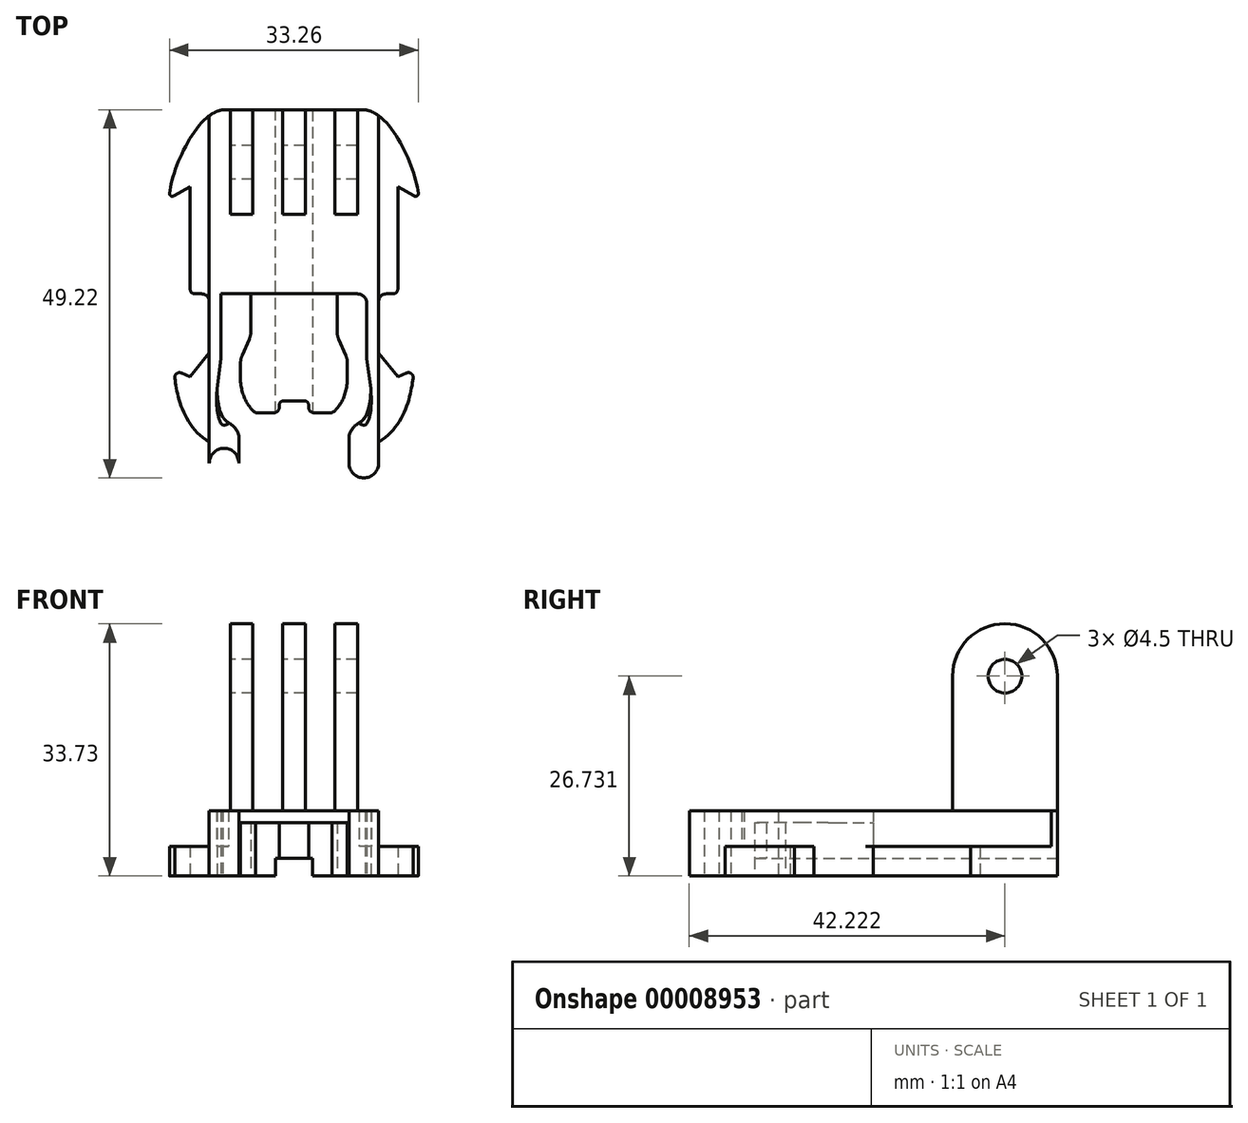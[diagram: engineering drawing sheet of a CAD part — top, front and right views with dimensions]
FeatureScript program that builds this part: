
annotation { "Feature Type Name" : "Feature", "Feature Type Description" : "" }
export const myFeature = defineFeature(function(context is Context, id is Id, definition is map)
    precondition{}
    {
        {
            var Q0;
            Q0=qCreatedBy(makeId("Top.planeOp"),FACE);
            var sketch = newSketch(context, id + "F0", { "sketchPlane" : qUnion([Q0])});
            skLineSegment(sketch, "E0.top", {"start": v(9.34, -29.6) * mm, "end": v(9.35, -29.6) * mm});
            skLineSegment(sketch, "E1", {"start": v(13.9, 9.3) * mm, "end": v(13.9, -4.35) * mm});
            skLineSegment(sketch, "E2", {"start": v(13.9, 9.3) * mm, "end": v(16.07, 8.1) * mm});
            skPoint(sketch, "E3", {"position": v(9.52, 19.62) * mm});
            skPoint(sketch, "E4", {"position": v(13.9, -4.98) * mm});
            skLineSegment(sketch, "E5", {"start": v(13.9, -16.1) * mm, "end": v(15.05, -15.57) * mm});
            skPoint(sketch, "E6", {"position": v(11.33, -24.83) * mm});
            skLineSegment(sketch, "E7", {"start": v(11.33, -24.83) * mm, "end": v(11.33, -27.62) * mm});
            skFitSpline(sketch, "E8", {"points": [v(11.33, -24.83) * mm, v(16.02, -15.53) * mm, v(15.35, -14) * mm], "startDerivative": vector(16.22, 10.26) * mm, "endDerivative": vector(-8.5, 1.39) * mm});
            skLineSegment(sketch, "E9", {"start": v(13.9, -16.1) * mm, "end": v(11.33, -12.92) * mm});
            skLineSegment(sketch, "E10", {"start": v(11.33, -12.92) * mm, "end": v(11.33, -6) * mm});
            skLineSegment(sketch, "E11", {"start": v(12.34, -4.98) * mm, "end": v(13.26, -4.98) * mm});
            skFitSpline(sketch, "E12", {"points": [v(9.52, 19.62) * mm, v(16.67, 7.77) * mm, v(15, 5.07) * mm], "startDerivative": vector(16.54, -1.98) * mm, "endDerivative": vector(-7.7, -6.84) * mm});
            skArc(sketch, "E13.filletArc", {"start": v(16.07, 8.1) * mm, "mid": v(16.46, 8.11) * mm, "end": v(16.63, 8.47) * mm});
            skArc(sketch, "E14.filletArc", {"start": v(13.26, -4.98) * mm, "mid": v(13.7, -4.8) * mm, "end": v(13.9, -4.35) * mm});
            skPoint(sketch, "E15.visualSharp", {"position": v(11.33, -4.98) * mm});
            skArc(sketch, "E15.filletArc", {"start": v(12.34, -4.98) * mm, "mid": v(11.62, -5.28) * mm, "end": v(11.33, -6) * mm});
            skPoint(sketch, "E16.newPointA", {"position": v(15.05, -15.57) * mm});
            skArc(sketch, "E16.filletArc", {"start": v(15.94, -16.23) * mm, "mid": v(15.69, -15.64) * mm, "end": v(15.05, -15.57) * mm});
            skLineSegment(sketch, "E17", {"start": v(0, 19.62) * mm, "end": v(0, -29.6) * mm, "construction": true});
            skLineSegment(sketch, "E18", {"start": v(9.74, -6.25) * mm, "end": v(9.74, -13.48) * mm});
            skLineSegment(sketch, "E19", {"start": v(11.33, -4.98) * mm, "end": v(12.34, -4.98) * mm, "construction": true});
            skLineSegment(sketch, "E20", {"start": v(5.77, -10.01) * mm, "end": v(5.77, -4.98) * mm});
            skLineSegment(sketch, "E21", {"start": v(7.14, -14.24) * mm, "end": v(7.14, -16.74) * mm});
            skLineSegment(sketch, "E22", {"start": v(11.33, -12.92) * mm, "end": v(11.33, -17.56) * mm, "construction": true});
            skLineSegment(sketch, "E23", {"start": v(0, -19.28) * mm, "end": v(1.35, -19.28) * mm});
            skLineSegment(sketch, "E24", {"start": v(1.98, -19.91) * mm, "end": v(1.98, -20.23) * mm});
            skLineSegment(sketch, "E25", {"start": v(2.62, -20.87) * mm, "end": v(5.12, -20.87) * mm});
            skLineSegment(sketch, "E26", {"start": v(5.98, -11.02) * mm, "end": v(6.93, -13.23) * mm});
            skLineSegment(sketch, "E27", {"start": v(9.75, -13.64) * mm, "end": v(10.27, -17.68) * mm});
            skPoint(sketch, "E28.visualSharp", {"position": v(9.74, -13.56) * mm});
            skArc(sketch, "E28.filletArc", {"start": v(9.74, -13.48) * mm, "mid": v(9.74, -13.56) * mm, "end": v(9.75, -13.64) * mm});
            skPoint(sketch, "E29.newPointA", {"position": v(9.92, -29.6) * mm});
            skPoint(sketch, "E29.newPointB", {"position": v(-16.67, -29.6) * mm});
            skPoint(sketch, "E30.newPointA", {"position": v(16.67, -29.6) * mm});
            skArc(sketch, "E30.filletArc", {"start": v(9.35, -29.6) * mm, "mid": v(10.75, -29.02) * mm, "end": v(11.33, -27.62) * mm});
            skPoint(sketch, "E31.visualSharp", {"position": v(5.77, -10.54) * mm});
            skArc(sketch, "E31.filletArc", {"start": v(5.77, -10.01) * mm, "mid": v(5.82, -10.53) * mm, "end": v(5.98, -11.02) * mm});
            skPoint(sketch, "E32.visualSharp", {"position": v(7.14, -13.72) * mm});
            skArc(sketch, "E32.filletArc", {"start": v(7.14, -14.24) * mm, "mid": v(7.1, -13.73) * mm, "end": v(6.93, -13.23) * mm});
            skPoint(sketch, "E33", {"position": v(7.14, -16.74) * mm});
            skPoint(sketch, "E34", {"position": v(5.12, -20.87) * mm});
            skPoint(sketch, "E35.visualSharp", {"position": v(1.98, -19.28) * mm});
            skArc(sketch, "E35.filletArc", {"start": v(1.98, -19.91) * mm, "mid": v(1.8, -19.47) * mm, "end": v(1.35, -19.28) * mm});
            skPoint(sketch, "E36.visualSharp", {"position": v(1.98, -20.87) * mm});
            skArc(sketch, "E36.filletArc", {"start": v(1.98, -20.23) * mm, "mid": v(2.17, -20.68) * mm, "end": v(2.62, -20.87) * mm});
            skFitSpline(sketch, "E37", {"points": [v(7.14, -16.74) * mm, v(5.12, -20.87) * mm, v(2.98, -21.27) * mm], "startDerivative": vector(-0.79, -9.29) * mm, "endDerivative": vector(-5.1, -0.3) * mm});
            skLineSegment(sketch, "E38.MirrorCS", {"start": v(0, -19.28) * mm, "end": v(-1.35, -19.28) * mm});
            skArc(sketch, "E39.MirrorCS", {"start": v(-1.98, -19.91) * mm, "mid": v(-1.8, -19.47) * mm, "end": v(-1.35, -19.28) * mm});
            skLineSegment(sketch, "E40.MirrorCS", {"start": v(-1.98, -19.91) * mm, "end": v(-1.98, -20.23) * mm});
            skArc(sketch, "E41.MirrorCS", {"start": v(-1.98, -20.23) * mm, "mid": v(-2.17, -20.68) * mm, "end": v(-2.62, -20.87) * mm});
            skLineSegment(sketch, "E42.MirrorCS", {"start": v(-2.62, -20.87) * mm, "end": v(-5.12, -20.87) * mm});
            skFitSpline(sketch, "E43.MirrorCS", {"points": [v(-7.14, -16.74) * mm, v(-5.12, -20.87) * mm, v(-2.98, -21.27) * mm], "startDerivative": vector(0.79, -9.29) * mm, "endDerivative": vector(5.1, -0.3) * mm});
            skLineSegment(sketch, "E44.MirrorCS", {"start": v(-7.14, -14.24) * mm, "end": v(-7.14, -16.74) * mm});
            skArc(sketch, "E45.MirrorCS", {"start": v(-7.14, -14.24) * mm, "mid": v(-7.1, -13.73) * mm, "end": v(-6.93, -13.23) * mm});
            skLineSegment(sketch, "E46.MirrorCS", {"start": v(-5.98, -11.02) * mm, "end": v(-6.93, -13.23) * mm});
            skArc(sketch, "E47.MirrorCS", {"start": v(-5.77, -10.01) * mm, "mid": v(-5.82, -10.53) * mm, "end": v(-5.98, -11.02) * mm});
            skLineSegment(sketch, "E48.MirrorCS", {"start": v(-5.77, -10.01) * mm, "end": v(-5.77, -4.98) * mm});
            skLineSegment(sketch, "E49.MirrorCS", {"start": v(-5.77, -4.98) * mm, "end": v(-9.74, -4.98) * mm});
            skLineSegment(sketch, "E50.MirrorCS", {"start": v(-9.74, -4.98) * mm, "end": v(-9.74, -13.48) * mm});
            skLineSegment(sketch, "E51.MirrorCS", {"start": v(-11.33, -12.92) * mm, "end": v(-11.33, -6) * mm});
            skArc(sketch, "E52.MirrorCS", {"start": v(-12.34, -4.98) * mm, "mid": v(-11.62, -5.28) * mm, "end": v(-11.33, -6) * mm});
            skLineSegment(sketch, "E53.MirrorCS", {"start": v(-12.34, -4.98) * mm, "end": v(-13.26, -4.98) * mm});
            skArc(sketch, "E54.MirrorCS", {"start": v(-13.26, -4.98) * mm, "mid": v(-13.7, -4.8) * mm, "end": v(-13.9, -4.35) * mm});
            skLineSegment(sketch, "E55.MirrorCS", {"start": v(-13.9, 9.3) * mm, "end": v(-13.9, -4.35) * mm});
            skLineSegment(sketch, "E56.MirrorCS", {"start": v(-13.9, 9.3) * mm, "end": v(-16.07, 8.1) * mm});
            skFitSpline(sketch, "E57.MirrorCS", {"points": [v(-9.53, 19.62) * mm, v(-16.67, 7.77) * mm, v(-15, 5.07) * mm], "startDerivative": vector(-16.54, -1.98) * mm, "endDerivative": vector(7.7, -6.84) * mm});
            skArc(sketch, "E58.MirrorCS", {"start": v(-16.07, 8.1) * mm, "mid": v(-16.46, 8.11) * mm, "end": v(-16.63, 8.47) * mm});
            skLineSegment(sketch, "E59.MirrorCS", {"start": v(-13.9, -16.1) * mm, "end": v(-11.33, -12.92) * mm});
            skLineSegment(sketch, "E60.MirrorCS", {"start": v(-13.9, -16.1) * mm, "end": v(-15.05, -15.57) * mm});
            skArc(sketch, "E61.MirrorCS", {"start": v(-15.94, -16.23) * mm, "mid": v(-15.69, -15.64) * mm, "end": v(-15.05, -15.57) * mm});
            skFitSpline(sketch, "E62.MirrorCS", {"points": [v(-11.33, -24.83) * mm, v(-16.02, -15.53) * mm, v(-15.35, -14) * mm], "startDerivative": vector(-16.22, 10.26) * mm, "endDerivative": vector(8.5, 1.39) * mm});
            skLineSegment(sketch, "E63.MirrorCS", {"start": v(-11.33, -24.83) * mm, "end": v(-11.33, -27.62) * mm});
            skArc(sketch, "E64.MirrorCS", {"start": v(-9.74, -13.48) * mm, "mid": v(-9.74, -13.56) * mm, "end": v(-9.75, -13.64) * mm});
            skPoint(sketch, "E65.orphan", {"position": v(-7.14, -20.87) * mm});
            skPoint(sketch, "E66.orphan", {"position": v(7.14, -20.87) * mm});
            skLineSegment(sketch, "E67", {"start": v(5.77, -4.98) * mm, "end": v(8.47, -4.98) * mm});
            skLineSegment(sketch, "E68", {"start": v(-9.52, 19.62) * mm, "end": v(9.52, 19.62) * mm});
            skPoint(sketch, "E69.third.point", {"position": v(-11.27, -29.57) * mm});
            skLineSegment(sketch, "E70", {"start": v(11.33, -12.92) * mm, "end": v(11.33, -26.48) * mm, "construction": true});
            skCircle(sketch, "E71", {"center": v(9.35, -27.62) * mm, "radius": 1.98 * mm});
            skLineSegment(sketch, "E72", {"start": v(7.36, -24.07) * mm, "end": v(7.36, -30.21) * mm});
            skFitSpline(sketch, "E73", {"points": [v(10.27, -17.68) * mm, v(9.08, -21.98) * mm, v(8.19, -22.6) * mm, v(7.36, -24.07) * mm], "startDerivative": vector(0, -16.5) * mm, "endDerivative": vector(-0.43, -5.66) * mm});
            skLineSegment(sketch, "E74.MirrorCS", {"start": v(-7.36, -24.07) * mm, "end": v(-7.36, -30.21) * mm});
            skCircle(sketch, "E75.MirrorC", {"center": v(-9.35, -27.62) * mm, "radius": 1.98 * mm});
            skFitSpline(sketch, "E76.MirrorCS", {"points": [v(-10.27, -17.68) * mm, v(-9.08, -21.98) * mm, v(-8.19, -22.6) * mm, v(-7.36, -24.07) * mm], "startDerivative": vector(0, -16.5) * mm, "endDerivative": vector(0.43, -5.66) * mm});
            skLineSegment(sketch, "E77.MirrorCS", {"start": v(-9.75, -13.64) * mm, "end": v(-10.27, -17.68) * mm});
            skPoint(sketch, "E78.visualSharp", {"position": v(9.74, -4.98) * mm});
            skArc(sketch, "E78.filletArc", {"start": v(9.74, -6.25) * mm, "mid": v(9.37, -5.36) * mm, "end": v(8.47, -4.98) * mm});
            skArc(sketch, "E79.MirrorCS", {"start": v(-9.74, -6.25) * mm, "mid": v(-9.37, -5.36) * mm, "end": v(-8.47, -4.98) * mm});
            skSolve(sketch);
        }
        {
            var Q0;
            Q0=makeQuery(id+"F0.imprint","IMPRINT",FACE,{"disambiguationData":[TD([[makeQuery(id+"F0.imprint","IMPRINT",EDGE,{"derivedFrom":sQuery(id+"F0.wireOp",EDGE,"E1")}),-1.0]])]});
            var Q1;
            {var subQ0=sQuery(id+"F0.wireOp",EDGE,"E75.MirrorC");var subQ1=makeQuery(id+"F0.imprint","INTERSECT",VERTEX,{"derivedFrom":[sQuery(id+"F0.wireOp",EDGE,"E63.MirrorCS"),subQ0]});Q1=makeQuery(id+"F0.imprint","IMPRINT",FACE,{"disambiguationData":[TD([[makeQuery(id+"F0.imprint","IMPRINT",EDGE,{"disambiguationData":[TD([[subQ1,1.0]])],"derivedFrom":subQ0}),-1.0]])]});}
            var Q2;
            {var subQ0=sQuery(id+"F0.wireOp",EDGE,"E71");var subQ1=makeQuery(id+"F0.imprint","INTERSECT",VERTEX,{"derivedFrom":[sQuery(id+"F0.wireOp",EDGE,"E7"),subQ0]});Q2=makeQuery(id+"F0.imprint","IMPRINT",FACE,{"disambiguationData":[TD([[makeQuery(id+"F0.imprint","IMPRINT",EDGE,{"disambiguationData":[TD([[subQ1,-1.0]])],"derivedFrom":subQ0}),1.0]])]});}
            var Q3;
            {var subQ3=sQuery(id+"F0.wireOp",EDGE,"E79.MirrorCS");Q3=makeQuery(id+"F0.imprint","IMPRINT",FACE,{"disambiguationData":[TD([[makeQuery(id+"F0.imprint","IMPRINT",EDGE,{"derivedFrom":subQ3}),1.0]])]});}
            extrude(context, id + "F1", {"entities" : qUnion([Q0, Q1, Q2, Q3]), "depth" : 3.97 * mm, "offsetDistance" : 25.4 * mm});
        }
        {
            var Q0;
            Q0=makeQuery(id+"F1.opExtrude","CAP_FACE",FACE,{"disambiguationData":[OSD([sQuery(id+"F0.wireOp",EDGE,"E1"),sQuery(id+"F0.wireOp",EDGE,"E2"),sQuery(id+"F0.wireOp",EDGE,"E5"),sQuery(id+"F0.wireOp",EDGE,"E7"),sQuery(id+"F0.wireOp",EDGE,"E8"),sQuery(id+"F0.wireOp",EDGE,"E9"),sQuery(id+"F0.wireOp",EDGE,"E10"),sQuery(id+"F0.wireOp",EDGE,"E11"),sQuery(id+"F0.wireOp",EDGE,"E12"),sQuery(id+"F0.wireOp",EDGE,"E13.filletArc"),sQuery(id+"F0.wireOp",EDGE,"E14.filletArc"),sQuery(id+"F0.wireOp",EDGE,"E15.filletArc"),sQuery(id+"F0.wireOp",EDGE,"E16.filletArc"),sQuery(id+"F0.wireOp",EDGE,"E18"),sQuery(id+"F0.wireOp",EDGE,"E20"),sQuery(id+"F0.wireOp",EDGE,"E21"),sQuery(id+"F0.wireOp",EDGE,"E23"),sQuery(id+"F0.wireOp",EDGE,"E24"),sQuery(id+"F0.wireOp",EDGE,"E25"),sQuery(id+"F0.wireOp",EDGE,"E26"),sQuery(id+"F0.wireOp",EDGE,"E27"),sQuery(id+"F0.wireOp",EDGE,"E28.filletArc"),sQuery(id+"F0.wireOp",EDGE,"E31.filletArc"),sQuery(id+"F0.wireOp",EDGE,"E32.filletArc"),sQuery(id+"F0.wireOp",EDGE,"E35.filletArc"),sQuery(id+"F0.wireOp",EDGE,"E36.filletArc"),sQuery(id+"F0.wireOp",EDGE,"E37"),sQuery(id+"F0.wireOp",EDGE,"E38.MirrorCS"),sQuery(id+"F0.wireOp",EDGE,"E39.MirrorCS"),sQuery(id+"F0.wireOp",EDGE,"E40.MirrorCS"),sQuery(id+"F0.wireOp",EDGE,"E41.MirrorCS"),sQuery(id+"F0.wireOp",EDGE,"E42.MirrorCS"),sQuery(id+"F0.wireOp",EDGE,"E43.MirrorCS"),sQuery(id+"F0.wireOp",EDGE,"E44.MirrorCS"),sQuery(id+"F0.wireOp",EDGE,"E45.MirrorCS"),sQuery(id+"F0.wireOp",EDGE,"E46.MirrorCS"),sQuery(id+"F0.wireOp",EDGE,"E47.MirrorCS"),sQuery(id+"F0.wireOp",EDGE,"E48.MirrorCS"),sQuery(id+"F0.wireOp",EDGE,"E49.MirrorCS"),sQuery(id+"F0.wireOp",EDGE,"E50.MirrorCS"),sQuery(id+"F0.wireOp",EDGE,"E51.MirrorCS"),sQuery(id+"F0.wireOp",EDGE,"E52.MirrorCS"),sQuery(id+"F0.wireOp",EDGE,"E53.MirrorCS"),sQuery(id+"F0.wireOp",EDGE,"E54.MirrorCS"),sQuery(id+"F0.wireOp",EDGE,"E55.MirrorCS"),sQuery(id+"F0.wireOp",EDGE,"E56.MirrorCS"),sQuery(id+"F0.wireOp",EDGE,"E57.MirrorCS"),sQuery(id+"F0.wireOp",EDGE,"E58.MirrorCS"),sQuery(id+"F0.wireOp",EDGE,"E59.MirrorCS"),sQuery(id+"F0.wireOp",EDGE,"E60.MirrorCS"),sQuery(id+"F0.wireOp",EDGE,"E61.MirrorCS"),sQuery(id+"F0.wireOp",EDGE,"E62.MirrorCS"),sQuery(id+"F0.wireOp",EDGE,"E63.MirrorCS"),sQuery(id+"F0.wireOp",EDGE,"E64.MirrorCS"),sQuery(id+"F0.wireOp",EDGE,"E67"),sQuery(id+"F0.wireOp",EDGE,"E68"),sQuery(id+"F0.wireOp",EDGE,"E71"),sQuery(id+"F0.wireOp",EDGE,"E72"),sQuery(id+"F0.wireOp",EDGE,"E73"),sQuery(id+"F0.wireOp",EDGE,"E74.MirrorCS"),sQuery(id+"F0.wireOp",EDGE,"E75.MirrorC"),sQuery(id+"F0.wireOp",EDGE,"E76.MirrorCS"),sQuery(id+"F0.wireOp",EDGE,"E77.MirrorCS")])],"isStart":false});
            var sketch = newSketch(context, id + "F2", { "sketchPlane" : qUnion([Q0])});
            skLineSegment(sketch, "E80.0.0", {"start": v(-7.36, -27.62) * mm, "end": v(-7.36, -24.07) * mm});
            skFitSpline(sketch, "E80.0.1", {"points": [v(-7.36, -20.86) * mm, v(-7.66, -20.68) * mm, v(-8.16, -21.5) * mm, v(-9.42, -22.57) * mm, v(-10.27, -20.49) * mm, v(-10.27, -17.68) * mm]});
            skLineSegment(sketch, "E80.0.2", {"start": v(-10.27, -17.68) * mm, "end": v(-9.75, -13.64) * mm});
            skArc(sketch, "E80.0.3", {"start": v(-9.75, -13.64) * mm, "mid": v(-9.74, -13.56) * mm, "end": v(-9.74, -13.48) * mm});
            skLineSegment(sketch, "E80.0.4", {"start": v(-9.74, -13.48) * mm, "end": v(-9.74, -6.25) * mm});
            skLineSegment(sketch, "E80.0.6", {"start": v(-5.77, -4.98) * mm, "end": v(-5.77, -10.01) * mm});
            skArc(sketch, "E80.0.7", {"start": v(-5.77, -10.01) * mm, "mid": v(-5.82, -10.53) * mm, "end": v(-5.98, -11.02) * mm});
            skLineSegment(sketch, "E80.0.8", {"start": v(-5.98, -11.02) * mm, "end": v(-6.93, -13.23) * mm});
            skArc(sketch, "E80.0.9", {"start": v(-6.93, -13.23) * mm, "mid": v(-7.1, -13.73) * mm, "end": v(-7.14, -14.24) * mm});
            skLineSegment(sketch, "E80.0.10", {"start": v(-7.14, -14.24) * mm, "end": v(-7.14, -16.74) * mm});
            skFitSpline(sketch, "E80.0.11", {"points": [v(-7.14, -16.74) * mm, v(-6.99, -18.58) * mm, v(-5.52, -21.4) * mm, v(-3.68, -21.23) * mm, v(-2.98, -21.27) * mm]});
            skLineSegment(sketch, "E80.0.12", {"start": v(-5.12, -20.87) * mm, "end": v(-2.62, -20.87) * mm});
            skArc(sketch, "E80.0.13", {"start": v(-2.62, -20.87) * mm, "mid": v(-2.17, -20.68) * mm, "end": v(-1.98, -20.23) * mm});
            skLineSegment(sketch, "E80.0.14", {"start": v(-1.98, -20.23) * mm, "end": v(-1.98, -19.91) * mm});
            skArc(sketch, "E80.0.15", {"start": v(-1.98, -19.91) * mm, "mid": v(-1.8, -19.47) * mm, "end": v(-1.35, -19.28) * mm});
            skLineSegment(sketch, "E80.0.16", {"start": v(-1.35, -19.28) * mm, "end": v(1.35, -19.28) * mm});
            skArc(sketch, "E80.0.17", {"start": v(1.35, -19.28) * mm, "mid": v(1.8, -19.47) * mm, "end": v(1.98, -19.91) * mm});
            skLineSegment(sketch, "E80.0.18", {"start": v(1.98, -19.91) * mm, "end": v(1.98, -20.23) * mm});
            skArc(sketch, "E80.0.19", {"start": v(1.98, -20.23) * mm, "mid": v(2.17, -20.68) * mm, "end": v(2.62, -20.87) * mm});
            skLineSegment(sketch, "E80.0.20", {"start": v(2.62, -20.87) * mm, "end": v(5.12, -20.87) * mm});
            skFitSpline(sketch, "E80.0.21", {"points": [v(2.98, -21.27) * mm, v(3.68, -21.23) * mm, v(5.52, -21.4) * mm, v(6.99, -18.58) * mm, v(7.14, -16.74) * mm]});
            skLineSegment(sketch, "E80.0.22", {"start": v(7.14, -16.74) * mm, "end": v(7.14, -14.24) * mm});
            skArc(sketch, "E80.0.23", {"start": v(7.14, -14.24) * mm, "mid": v(7.1, -13.73) * mm, "end": v(6.93, -13.23) * mm});
            skLineSegment(sketch, "E80.0.24", {"start": v(6.93, -13.23) * mm, "end": v(5.98, -11.02) * mm});
            skArc(sketch, "E80.0.25", {"start": v(5.98, -11.02) * mm, "mid": v(5.82, -10.53) * mm, "end": v(5.77, -10.01) * mm});
            skLineSegment(sketch, "E80.0.26", {"start": v(5.77, -10.01) * mm, "end": v(5.77, -4.98) * mm});
            skLineSegment(sketch, "E80.0.27", {"start": v(5.77, -4.98) * mm, "end": v(8.47, -4.98) * mm});
            skArc(sketch, "E80.0.29", {"start": v(9.74, -13.48) * mm, "mid": v(9.74, -13.56) * mm, "end": v(9.75, -13.64) * mm});
            skLineSegment(sketch, "E80.0.30", {"start": v(9.75, -13.64) * mm, "end": v(10.27, -17.68) * mm});
            skFitSpline(sketch, "E80.0.31", {"points": [v(10.27, -17.68) * mm, v(10.27, -20.49) * mm, v(9.42, -22.57) * mm, v(8.16, -21.5) * mm, v(7.66, -20.68) * mm, v(7.36, -20.86) * mm]});
            skLineSegment(sketch, "E80.0.32", {"start": v(7.36, -24.07) * mm, "end": v(7.36, -27.62) * mm});
            skArc(sketch, "E80.0.33", {"start": v(7.36, -27.62) * mm, "mid": v(9.35, -29.6) * mm, "end": v(11.33, -27.61) * mm});
            skLineSegment(sketch, "E80.0.34", {"start": v(11.33, -27.61) * mm, "end": v(11.33, -24.83) * mm});
            skFitSpline(sketch, "E80.0.35", {"points": [v(11.33, -24.83) * mm, v(15.17, -22.4) * mm, v(17.46, -15.3) * mm, v(16.17, -14.14) * mm, v(15.35, -14) * mm]});
            skArc(sketch, "E80.0.36", {"start": v(15.94, -16.23) * mm, "mid": v(15.69, -15.64) * mm, "end": v(15.05, -15.57) * mm});
            skLineSegment(sketch, "E80.0.37", {"start": v(15.05, -15.57) * mm, "end": v(13.9, -16.1) * mm});
            skLineSegment(sketch, "E80.0.38", {"start": v(13.9, -16.1) * mm, "end": v(11.33, -12.92) * mm});
            skLineSegment(sketch, "E80.0.39", {"start": v(11.33, -12.92) * mm, "end": v(11.33, -6) * mm});
            skArc(sketch, "E80.0.40", {"start": v(11.33, -6) * mm, "mid": v(11.62, -5.28) * mm, "end": v(12.34, -4.98) * mm});
            skLineSegment(sketch, "E80.0.41", {"start": v(12.34, -4.98) * mm, "end": v(13.26, -4.98) * mm});
            skArc(sketch, "E80.0.42", {"start": v(13.26, -4.98) * mm, "mid": v(13.7, -4.8) * mm, "end": v(13.9, -4.35) * mm});
            skLineSegment(sketch, "E80.0.43", {"start": v(13.9, -4.35) * mm, "end": v(13.9, 9.3) * mm});
            skLineSegment(sketch, "E80.0.44", {"start": v(13.9, 9.3) * mm, "end": v(16.07, 8.1) * mm});
            skArc(sketch, "E80.0.45", {"start": v(16.07, 8.1) * mm, "mid": v(16.46, 8.11) * mm, "end": v(16.63, 8.47) * mm});
            skFitSpline(sketch, "E80.0.46", {"points": [v(15, 5.07) * mm, v(15.83, 5.8) * mm, v(18.36, 7.08) * mm, v(13.25, 19.18) * mm, v(9.52, 19.62) * mm]});
            skLineSegment(sketch, "E80.0.47", {"start": v(9.52, 19.62) * mm, "end": v(-9.52, 19.62) * mm});
            skFitSpline(sketch, "E80.0.48", {"points": [v(-9.53, 19.62) * mm, v(-13.25, 19.18) * mm, v(-18.36, 7.08) * mm, v(-15.83, 5.8) * mm, v(-15, 5.07) * mm]});
            skArc(sketch, "E80.0.49", {"start": v(-16.63, 8.47) * mm, "mid": v(-16.46, 8.11) * mm, "end": v(-16.07, 8.1) * mm});
            skLineSegment(sketch, "E80.0.50", {"start": v(-16.07, 8.1) * mm, "end": v(-13.9, 9.3) * mm});
            skLineSegment(sketch, "E80.0.51", {"start": v(-13.9, 9.3) * mm, "end": v(-13.9, -4.35) * mm});
            skArc(sketch, "E80.0.52", {"start": v(-13.9, -4.35) * mm, "mid": v(-13.7, -4.8) * mm, "end": v(-13.26, -4.98) * mm});
            skLineSegment(sketch, "E80.0.53", {"start": v(-13.26, -4.98) * mm, "end": v(-12.34, -4.98) * mm});
            skArc(sketch, "E80.0.54", {"start": v(-12.34, -4.98) * mm, "mid": v(-11.62, -5.28) * mm, "end": v(-11.33, -6) * mm});
            skLineSegment(sketch, "E80.0.55", {"start": v(-11.33, -6) * mm, "end": v(-11.33, -12.92) * mm});
            skLineSegment(sketch, "E80.0.56", {"start": v(-11.33, -12.92) * mm, "end": v(-13.9, -16.1) * mm});
            skLineSegment(sketch, "E80.0.57", {"start": v(-13.9, -16.1) * mm, "end": v(-15.05, -15.57) * mm});
            skArc(sketch, "E80.0.58", {"start": v(-15.05, -15.57) * mm, "mid": v(-15.69, -15.64) * mm, "end": v(-15.94, -16.23) * mm});
            skFitSpline(sketch, "E80.0.59", {"points": [v(-15.35, -14) * mm, v(-16.17, -14.14) * mm, v(-17.46, -15.3) * mm, v(-15.17, -22.4) * mm, v(-11.33, -24.83) * mm]});
            skLineSegment(sketch, "E80.0.60", {"start": v(-11.33, -24.83) * mm, "end": v(-11.33, -27.61) * mm});
            skArc(sketch, "E80.0.61", {"start": v(-11.33, -27.61) * mm, "mid": v(-9.35, -29.6) * mm, "end": v(-7.36, -27.62) * mm});
            skLineSegment(sketch, "E81", {"start": v(11.33, -12.92) * mm, "end": v(11.33, -24.83) * mm});
            skLineSegment(sketch, "E82", {"start": v(11.33, -6) * mm, "end": v(11.33, 18.83) * mm});
            skLineSegment(sketch, "E83.MirrorCS", {"start": v(-11.33, -6) * mm, "end": v(-11.33, 18.83) * mm});
            skLineSegment(sketch, "E84.MirrorCS", {"start": v(-11.33, -12.92) * mm, "end": v(-11.33, -24.83) * mm});
            skLineSegment(sketch, "E85", {"start": v(-5.77, -4.98) * mm, "end": v(5.77, -4.98) * mm});
            skSolve(sketch);
        }
        {
            var Q0;
            Q0=makeQuery(id+"F2.imprint","IMPRINT",FACE,{"disambiguationData":[TD([[makeQuery(id+"F2.imprint","IMPRINT",EDGE,{"derivedFrom":sQuery(id+"F2.wireOp",EDGE,"E80.0.0")}),-1.0]])]});
            extrude(context, id + "F3", {"entities" : qUnion([Q0]), "operationType" : NewBodyOperationType.ADD, "depth" : 4.76 * mm, "offsetDistance" : 25.4 * mm});
        }
        {
            var Q0;
            {var subQ0=sQuery(id+"F0.wireOp",EDGE,"E48.MirrorCS");var subQ1=sQuery(id+"F0.wireOp",EDGE,"E47.MirrorCS");var subQ2=sQuery(id+"F0.wireOp",EDGE,"E46.MirrorCS");var subQ3=sQuery(id+"F0.wireOp",EDGE,"E45.MirrorCS");var subQ4=sQuery(id+"F0.wireOp",EDGE,"E49.MirrorCS");var subQ5=sQuery(id+"F0.wireOp",EDGE,"E44.MirrorCS");var subQ6=sQuery(id+"F0.wireOp",EDGE,"E43.MirrorCS");var subQ7=sQuery(id+"F0.wireOp",EDGE,"E42.MirrorCS");var subQ8=sQuery(id+"F0.wireOp",EDGE,"E41.MirrorCS");var subQ9=sQuery(id+"F0.wireOp",EDGE,"E40.MirrorCS");var subQ10=sQuery(id+"F0.wireOp",EDGE,"E39.MirrorCS");var subQ11=sQuery(id+"F0.wireOp",EDGE,"E37");var subQ12=sQuery(id+"F0.wireOp",EDGE,"E24");var subQ13=sQuery(id+"F0.wireOp",EDGE,"E38.MirrorCS");var subQ14=sQuery(id+"F0.wireOp",EDGE,"E23");var subQ15=sQuery(id+"F0.wireOp",EDGE,"E21");var subQ16=sQuery(id+"F0.wireOp",EDGE,"E20");var subQ17=sQuery(id+"F0.wireOp",EDGE,"E36.filletArc");var subQ18=sQuery(id+"F0.wireOp",EDGE,"E25");var subQ19=sQuery(id+"F0.wireOp",EDGE,"E26");var subQ20=sQuery(id+"F0.wireOp",EDGE,"E31.filletArc");var subQ21=sQuery(id+"F0.wireOp",EDGE,"E32.filletArc");var subQ22=sQuery(id+"F0.wireOp",EDGE,"E35.filletArc");var subQ23=sQuery(id+"F0.wireOp",EDGE,"E67");Q0=makeQuery(id+"F3.boolean.opBoolean","SPLIT",FACE,{"disambiguationData":[TD([makeQuery(id+"F1.opExtrude","SWEPT_FACE",FACE,{"disambiguationData":[OSD([subQ16])]})])],"derivedFrom":makeQuery(id+"F1.opExtrude","CAP_FACE",FACE,{"disambiguationData":[OSD([sQuery(id+"F0.wireOp",EDGE,"E1"),sQuery(id+"F0.wireOp",EDGE,"E2"),sQuery(id+"F0.wireOp",EDGE,"E5"),sQuery(id+"F0.wireOp",EDGE,"E7"),sQuery(id+"F0.wireOp",EDGE,"E8"),sQuery(id+"F0.wireOp",EDGE,"E9"),sQuery(id+"F0.wireOp",EDGE,"E10"),sQuery(id+"F0.wireOp",EDGE,"E11"),sQuery(id+"F0.wireOp",EDGE,"E12"),sQuery(id+"F0.wireOp",EDGE,"E13.filletArc"),sQuery(id+"F0.wireOp",EDGE,"E14.filletArc"),sQuery(id+"F0.wireOp",EDGE,"E15.filletArc"),sQuery(id+"F0.wireOp",EDGE,"E16.filletArc"),sQuery(id+"F0.wireOp",EDGE,"E18"),subQ16,subQ15,subQ14,subQ12,subQ18,subQ19,sQuery(id+"F0.wireOp",EDGE,"E27"),sQuery(id+"F0.wireOp",EDGE,"E28.filletArc"),subQ20,subQ21,subQ22,subQ17,subQ11,subQ13,subQ10,subQ9,subQ8,subQ7,subQ6,subQ5,subQ3,subQ2,subQ1,subQ0,subQ4,sQuery(id+"F0.wireOp",EDGE,"E50.MirrorCS"),sQuery(id+"F0.wireOp",EDGE,"E51.MirrorCS"),sQuery(id+"F0.wireOp",EDGE,"E52.MirrorCS"),sQuery(id+"F0.wireOp",EDGE,"E53.MirrorCS"),sQuery(id+"F0.wireOp",EDGE,"E54.MirrorCS"),sQuery(id+"F0.wireOp",EDGE,"E55.MirrorCS"),sQuery(id+"F0.wireOp",EDGE,"E56.MirrorCS"),sQuery(id+"F0.wireOp",EDGE,"E57.MirrorCS"),sQuery(id+"F0.wireOp",EDGE,"E58.MirrorCS"),sQuery(id+"F0.wireOp",EDGE,"E59.MirrorCS"),sQuery(id+"F0.wireOp",EDGE,"E60.MirrorCS"),sQuery(id+"F0.wireOp",EDGE,"E61.MirrorCS"),sQuery(id+"F0.wireOp",EDGE,"E62.MirrorCS"),sQuery(id+"F0.wireOp",EDGE,"E63.MirrorCS"),sQuery(id+"F0.wireOp",EDGE,"E64.MirrorCS"),subQ23,sQuery(id+"F0.wireOp",EDGE,"E68"),sQuery(id+"F0.wireOp",EDGE,"E71"),sQuery(id+"F0.wireOp",EDGE,"E72"),sQuery(id+"F0.wireOp",EDGE,"E73"),sQuery(id+"F0.wireOp",EDGE,"E74.MirrorCS"),sQuery(id+"F0.wireOp",EDGE,"E75.MirrorC"),sQuery(id+"F0.wireOp",EDGE,"E76.MirrorCS"),sQuery(id+"F0.wireOp",EDGE,"E77.MirrorCS"),sQuery(id+"F0.wireOp",EDGE,"E78.filletArc"),sQuery(id+"F0.wireOp",EDGE,"E79.MirrorCS")])],"isStart":false})});}
            extrude(context, id + "F4", {"entities" : qUnion([Q0]), "operationType" : NewBodyOperationType.ADD, "depth" : 3.17 * mm, "offsetDistance" : 25.4 * mm});
        }
        {
            var Q0;
            Q0=makeQuery(id+"F0.imprint","IMPRINT",FACE,{"disambiguationData":[TD([[makeQuery(id+"F0.imprint","IMPRINT",EDGE,{"derivedFrom":sQuery(id+"F0.wireOp",EDGE,"E1")}),-1.0]])]});
            var sketch = newSketch(context, id + "F5", { "sketchPlane" : qUnion([Q0])});
            skLineSegment(sketch, "E86.0", {"start": v(-1.98, -19.91) * mm, "end": v(-1.98, -20.23) * mm});
            skLineSegment(sketch, "E87.0", {"start": v(1.98, -19.91) * mm, "end": v(1.98, -20.23) * mm});
            skLineSegment(sketch, "E88", {"start": v(-1.98, -19.91) * mm, "end": v(-1.98, 19.62) * mm});
            skLineSegment(sketch, "E89.MirrorCS", {"start": v(1.98, -19.91) * mm, "end": v(1.98, 19.62) * mm});
            skLineSegment(sketch, "E90", {"start": v(-1.98, 19.62) * mm, "end": v(1.98, 19.62) * mm});
            skLineSegment(sketch, "E91", {"start": v(-1.98, -20.23) * mm, "end": v(1.98, -20.23) * mm});
            skLineSegment(sketch, "E92.0", {"start": v(-9.52, 19.62) * mm, "end": v(9.52, 19.62) * mm});
            skLineSegment(sketch, "E93.0.0", {"start": v(-9.74, -6.25) * mm, "end": v(-9.74, -4.98) * mm});
            skLineSegment(sketch, "E93.0.1", {"start": v(-9.74, -4.98) * mm, "end": v(-8.47, -4.98) * mm});
            skLineSegment(sketch, "E93.0.2", {"start": v(-8.47, -4.98) * mm, "end": v(-5.77, -4.98) * mm});
            skLineSegment(sketch, "E93.0.3", {"start": v(-5.77, -4.98) * mm, "end": v(-5.77, -10.01) * mm});
            skArc(sketch, "E93.0.4", {"start": v(-5.77, -10.01) * mm, "mid": v(-5.82, -10.53) * mm, "end": v(-5.98, -11.02) * mm});
            skLineSegment(sketch, "E93.0.5", {"start": v(-5.98, -11.02) * mm, "end": v(-6.93, -13.23) * mm});
            skArc(sketch, "E93.0.6", {"start": v(-6.93, -13.23) * mm, "mid": v(-7.1, -13.73) * mm, "end": v(-7.14, -14.24) * mm});
            skLineSegment(sketch, "E93.0.7", {"start": v(-7.14, -14.24) * mm, "end": v(-7.14, -16.74) * mm});
            skFitSpline(sketch, "E93.0.8", {"points": [v(-7.14, -16.74) * mm, v(-6.99, -18.58) * mm, v(-5.52, -21.4) * mm, v(-3.68, -21.23) * mm, v(-2.98, -21.27) * mm]});
            skLineSegment(sketch, "E93.0.9", {"start": v(-5.12, -20.87) * mm, "end": v(-2.62, -20.87) * mm});
            skArc(sketch, "E93.0.10", {"start": v(-2.62, -20.87) * mm, "mid": v(-2.17, -20.68) * mm, "end": v(-1.98, -20.23) * mm});
            skLineSegment(sketch, "E93.0.11", {"start": v(-1.98, -20.23) * mm, "end": v(-1.98, -19.91) * mm});
            skArc(sketch, "E93.0.12", {"start": v(-1.98, -19.91) * mm, "mid": v(-1.8, -19.47) * mm, "end": v(-1.35, -19.28) * mm});
            skLineSegment(sketch, "E93.0.13", {"start": v(-1.35, -19.28) * mm, "end": v(0, -19.28) * mm});
            skLineSegment(sketch, "E93.0.14", {"start": v(0, -19.28) * mm, "end": v(1.35, -19.28) * mm});
            skArc(sketch, "E93.0.15", {"start": v(1.35, -19.28) * mm, "mid": v(1.8, -19.47) * mm, "end": v(1.98, -19.91) * mm});
            skArc(sketch, "E93.0.17", {"start": v(1.98, -20.23) * mm, "mid": v(2.17, -20.68) * mm, "end": v(2.62, -20.87) * mm});
            skLineSegment(sketch, "E93.0.18", {"start": v(2.62, -20.87) * mm, "end": v(5.12, -20.87) * mm});
            skFitSpline(sketch, "E93.0.19", {"points": [v(2.98, -21.27) * mm, v(3.68, -21.23) * mm, v(5.52, -21.4) * mm, v(6.99, -18.58) * mm, v(7.14, -16.74) * mm]});
            skLineSegment(sketch, "E93.0.20", {"start": v(7.14, -16.74) * mm, "end": v(7.14, -14.24) * mm});
            skArc(sketch, "E93.0.21", {"start": v(7.14, -14.24) * mm, "mid": v(7.1, -13.73) * mm, "end": v(6.93, -13.23) * mm});
            skLineSegment(sketch, "E93.0.22", {"start": v(6.93, -13.23) * mm, "end": v(5.98, -11.02) * mm});
            skArc(sketch, "E93.0.23", {"start": v(5.98, -11.02) * mm, "mid": v(5.82, -10.53) * mm, "end": v(5.77, -10.01) * mm});
            skLineSegment(sketch, "E93.0.24", {"start": v(5.77, -10.01) * mm, "end": v(5.77, -4.98) * mm});
            skLineSegment(sketch, "E93.0.25", {"start": v(5.77, -4.98) * mm, "end": v(8.47, -4.98) * mm});
            skArc(sketch, "E93.0.26", {"start": v(8.47, -4.98) * mm, "mid": v(9.37, -5.36) * mm, "end": v(9.74, -6.25) * mm});
            skLineSegment(sketch, "E93.0.27", {"start": v(9.74, -6.25) * mm, "end": v(9.74, -13.48) * mm});
            skArc(sketch, "E93.0.28", {"start": v(9.74, -13.48) * mm, "mid": v(9.74, -13.56) * mm, "end": v(9.75, -13.64) * mm});
            skLineSegment(sketch, "E93.0.29", {"start": v(9.75, -13.64) * mm, "end": v(10.27, -17.68) * mm});
            skFitSpline(sketch, "E93.0.30", {"points": [v(10.27, -17.68) * mm, v(10.27, -20.29) * mm, v(9.38, -22.03) * mm, v(8.13, -22.46) * mm, v(7.4, -23.52) * mm, v(7.36, -24.07) * mm]});
            skLineSegment(sketch, "E93.0.31", {"start": v(7.36, -24.07) * mm, "end": v(7.36, -27.62) * mm});
            skArc(sketch, "E93.0.32", {"start": v(7.36, -27.62) * mm, "mid": v(9.34, -25.64) * mm, "end": v(11.33, -27.61) * mm});
            skLineSegment(sketch, "E93.0.33", {"start": v(11.33, -27.61) * mm, "end": v(11.33, -24.83) * mm});
            skFitSpline(sketch, "E93.0.34", {"points": [v(11.33, -24.83) * mm, v(15.17, -22.4) * mm, v(17.46, -15.3) * mm, v(16.17, -14.14) * mm, v(15.35, -14) * mm]});
            skArc(sketch, "E93.0.35", {"start": v(15.94, -16.23) * mm, "mid": v(15.69, -15.64) * mm, "end": v(15.05, -15.57) * mm});
            skLineSegment(sketch, "E93.0.36", {"start": v(15.05, -15.57) * mm, "end": v(13.9, -16.1) * mm});
            skLineSegment(sketch, "E93.0.37", {"start": v(13.9, -16.1) * mm, "end": v(11.33, -12.92) * mm});
            skLineSegment(sketch, "E93.0.38", {"start": v(11.33, -12.92) * mm, "end": v(11.33, -6) * mm});
            skArc(sketch, "E93.0.39", {"start": v(11.33, -6) * mm, "mid": v(11.62, -5.28) * mm, "end": v(12.34, -4.98) * mm});
            skLineSegment(sketch, "E93.0.40", {"start": v(12.34, -4.98) * mm, "end": v(13.26, -4.98) * mm});
            skArc(sketch, "E93.0.41", {"start": v(13.26, -4.98) * mm, "mid": v(13.7, -4.8) * mm, "end": v(13.9, -4.35) * mm});
            skLineSegment(sketch, "E93.0.42", {"start": v(13.9, -4.35) * mm, "end": v(13.9, 9.3) * mm});
            skLineSegment(sketch, "E93.0.43", {"start": v(13.9, 9.3) * mm, "end": v(16.07, 8.1) * mm});
            skArc(sketch, "E93.0.44", {"start": v(16.07, 8.1) * mm, "mid": v(16.46, 8.11) * mm, "end": v(16.63, 8.47) * mm});
            skFitSpline(sketch, "E93.0.45", {"points": [v(15, 5.07) * mm, v(15.83, 5.8) * mm, v(18.36, 7.08) * mm, v(13.25, 19.18) * mm, v(9.52, 19.62) * mm]});
            skLineSegment(sketch, "E93.0.46", {"start": v(9.52, 19.62) * mm, "end": v(-9.52, 19.62) * mm});
            skFitSpline(sketch, "E93.0.47", {"points": [v(-9.53, 19.62) * mm, v(-13.25, 19.18) * mm, v(-18.36, 7.08) * mm, v(-15.83, 5.8) * mm, v(-15, 5.07) * mm]});
            skArc(sketch, "E93.0.48", {"start": v(-16.63, 8.47) * mm, "mid": v(-16.46, 8.11) * mm, "end": v(-16.07, 8.1) * mm});
            skLineSegment(sketch, "E93.0.49", {"start": v(-16.07, 8.1) * mm, "end": v(-13.9, 9.3) * mm});
            skLineSegment(sketch, "E93.0.50", {"start": v(-13.9, 9.3) * mm, "end": v(-13.9, -4.35) * mm});
            skArc(sketch, "E93.0.51", {"start": v(-13.9, -4.35) * mm, "mid": v(-13.7, -4.8) * mm, "end": v(-13.26, -4.98) * mm});
            skLineSegment(sketch, "E93.0.52", {"start": v(-13.26, -4.98) * mm, "end": v(-12.34, -4.98) * mm});
            skArc(sketch, "E93.0.53", {"start": v(-12.34, -4.98) * mm, "mid": v(-11.62, -5.28) * mm, "end": v(-11.33, -6) * mm});
            skLineSegment(sketch, "E93.0.54", {"start": v(-11.33, -6) * mm, "end": v(-11.33, -12.92) * mm});
            skLineSegment(sketch, "E93.0.55", {"start": v(-11.33, -12.92) * mm, "end": v(-13.9, -16.1) * mm});
            skLineSegment(sketch, "E93.0.56", {"start": v(-13.9, -16.1) * mm, "end": v(-15.05, -15.57) * mm});
            skArc(sketch, "E93.0.57", {"start": v(-15.05, -15.57) * mm, "mid": v(-15.69, -15.64) * mm, "end": v(-15.94, -16.23) * mm});
            skFitSpline(sketch, "E93.0.58", {"points": [v(-15.35, -14) * mm, v(-16.17, -14.14) * mm, v(-17.46, -15.3) * mm, v(-15.17, -22.4) * mm, v(-11.33, -24.83) * mm]});
            skLineSegment(sketch, "E93.0.59", {"start": v(-11.33, -24.83) * mm, "end": v(-11.33, -27.61) * mm});
            skArc(sketch, "E93.0.60", {"start": v(-11.33, -27.61) * mm, "mid": v(-9.34, -25.64) * mm, "end": v(-7.36, -27.62) * mm});
            skLineSegment(sketch, "E93.0.61", {"start": v(-7.36, -27.62) * mm, "end": v(-7.36, -24.07) * mm});
            skFitSpline(sketch, "E93.0.62", {"points": [v(-7.36, -24.07) * mm, v(-7.4, -23.52) * mm, v(-8.13, -22.46) * mm, v(-9.38, -22.03) * mm, v(-10.27, -20.29) * mm, v(-10.27, -17.68) * mm]});
            skLineSegment(sketch, "E93.0.63", {"start": v(-10.27, -17.68) * mm, "end": v(-9.75, -13.64) * mm});
            skArc(sketch, "E93.0.64", {"start": v(-9.75, -13.64) * mm, "mid": v(-9.74, -13.56) * mm, "end": v(-9.74, -13.48) * mm});
            skLineSegment(sketch, "E93.0.65", {"start": v(-9.74, -13.48) * mm, "end": v(-9.74, -6.25) * mm});
            skLineSegment(sketch, "E94.0", {"start": v(2.5, -19.91) * mm, "end": v(2.5, 19.62) * mm});
            skLineSegment(sketch, "E95", {"start": v(2.5, -19.91) * mm, "end": v(2.5, -20.85) * mm});
            skLineSegment(sketch, "E96", {"start": v(2.5, 19.62) * mm, "end": v(1.98, 19.62) * mm});
            skLineSegment(sketch, "E97.MirrorCS", {"start": v(-2.5, -19.91) * mm, "end": v(-2.5, 19.62) * mm});
            skLineSegment(sketch, "E98.MirrorCS", {"start": v(-2.5, -19.91) * mm, "end": v(-2.5, -20.85) * mm});
            skLineSegment(sketch, "E99", {"start": v(-2.5, 19.62) * mm, "end": v(-1.98, 19.62) * mm});
            skSolve(sketch);
        }
        {
            var Q0;
            Q0=makeQuery(id+"F5.imprint","IMPRINT",FACE,{"disambiguationData":[TD([[makeQuery(id+"F5.imprint","IMPRINT",EDGE,{"derivedFrom":sQuery(id+"F5.wireOp",EDGE,"E88")}),-1.0]])]});
            var Q1;
            {var subQ4=sQuery(id+"F5.wireOp",EDGE,"E86.0");Q1=makeQuery(id+"F5.imprint","IMPRINT",FACE,{"disambiguationData":[TD([[makeQuery(id+"F5.imprint","IMPRINT",EDGE,{"derivedFrom":subQ4}),-1.0]])]});}
            var Q2;
            {var subQ4=sQuery(id+"F5.wireOp",EDGE,"E87.0");Q2=makeQuery(id+"F5.imprint","IMPRINT",FACE,{"disambiguationData":[TD([[makeQuery(id+"F5.imprint","IMPRINT",EDGE,{"derivedFrom":subQ4}),1.0]])]});}
            extrude(context, id + "F6", {"entities" : qUnion([Q0, Q1, Q2]), "operationType" : NewBodyOperationType.REMOVE, "depth" : 2.38 * mm, "offsetDistance" : 25.4 * mm});
        }
        {
            var Q0;
            Q0=makeQuery(id+"F3.opExtrude","CAP_FACE",FACE,{"disambiguationData":[OSD([sQuery(id+"F0.wireOp",EDGE,"E18"),sQuery(id+"F0.wireOp",EDGE,"E49.MirrorCS"),sQuery(id+"F0.wireOp",EDGE,"E78.filletArc"),sQuery(id+"F0.wireOp",EDGE,"E79.MirrorCS"),sQuery(id+"F2.wireOp",EDGE,"E80.0.0"),sQuery(id+"F2.wireOp",EDGE,"E80.0.1"),sQuery(id+"F2.wireOp",EDGE,"E80.0.2"),sQuery(id+"F2.wireOp",EDGE,"E80.0.3"),sQuery(id+"F2.wireOp",EDGE,"E80.0.4"),sQuery(id+"F2.wireOp",EDGE,"E80.0.27"),sQuery(id+"F2.wireOp",EDGE,"E80.0.29"),sQuery(id+"F2.wireOp",EDGE,"E80.0.30"),sQuery(id+"F2.wireOp",EDGE,"E80.0.31"),sQuery(id+"F2.wireOp",EDGE,"E80.0.32"),sQuery(id+"F2.wireOp",EDGE,"E80.0.33"),sQuery(id+"F2.wireOp",EDGE,"E80.0.34"),sQuery(id+"F2.wireOp",EDGE,"E80.0.39"),sQuery(id+"F2.wireOp",EDGE,"E80.0.46"),sQuery(id+"F2.wireOp",EDGE,"E80.0.47"),sQuery(id+"F2.wireOp",EDGE,"E80.0.48"),sQuery(id+"F2.wireOp",EDGE,"E80.0.55"),sQuery(id+"F2.wireOp",EDGE,"E80.0.60"),sQuery(id+"F2.wireOp",EDGE,"E80.0.61"),sQuery(id+"F2.wireOp",EDGE,"E81"),sQuery(id+"F2.wireOp",EDGE,"E82"),sQuery(id+"F2.wireOp",EDGE,"E83.MirrorCS"),sQuery(id+"F2.wireOp",EDGE,"E84.MirrorCS"),sQuery(id+"F2.wireOp",EDGE,"E85")])],"isStart":false});
            var sketch = newSketch(context, id + "F7", { "sketchPlane" : qUnion([Q0])});
            skLineSegment(sketch, "E100.bottom", {"start": v(-7.5, 19.62) * mm, "end": v(8.5, 19.62) * mm});
            skLineSegment(sketch, "E100.top", {"start": v(-7.5, 5.62) * mm, "end": v(8.5, 5.62) * mm});
            skLineSegment(sketch, "E100.right", {"start": v(8.5, 19.62) * mm, "end": v(8.5, 5.62) * mm});
            skLineSegment(sketch, "E101", {"start": v(1.5, 19.62) * mm, "end": v(1.5, 5.62) * mm});
            skLineSegment(sketch, "E102", {"start": v(5.5, 19.62) * mm, "end": v(5.5, 5.62) * mm});
            skLineSegment(sketch, "E103.MirrorCS", {"start": v(-1.5, 19.62) * mm, "end": v(-1.5, 5.62) * mm});
            skLineSegment(sketch, "E104.MirrorCS", {"start": v(-5.5, 19.62) * mm, "end": v(-5.5, 5.62) * mm});
            skLineSegment(sketch, "E105.MirrorCS", {"start": v(-8.5, 19.62) * mm, "end": v(-8.5, 5.62) * mm});
            skLineSegment(sketch, "E106", {"start": v(-8.5, 5.62) * mm, "end": v(-7.5, 5.62) * mm});
            skSolve(sketch);
        }
        {
            var Q0;
            {var subQ0=sQuery(id+"F7.wireOp",EDGE,"E100.left");Q0=makeQuery(id+"F7.imprint","IMPRINT",FACE,{"disambiguationData":[TD([[makeQuery(id+"F7.imprint","IMPRINT",EDGE,{"derivedFrom":subQ0}),1.0]])]});}
            var Q1;
            {var subQ0=sQuery(id+"F7.wireOp",EDGE,"39361f40-fd9d-4920-b611-31b20c453240.1.0.0");Q1=makeQuery(id+"F7.imprint","IMPRINT",FACE,{"disambiguationData":[TD([[makeQuery(id+"F7.imprint","IMPRINT",EDGE,{"derivedFrom":subQ0}),1.0]])]});}
            var Q2;
            {var subQ0=sQuery(id+"F7.wireOp",EDGE,"E100.right");Q2=makeQuery(id+"F7.imprint","IMPRINT",FACE,{"disambiguationData":[TD([[makeQuery(id+"F7.imprint","IMPRINT",EDGE,{"derivedFrom":subQ0}),-1.0]])]});}
            var Q3;
            {var subQ0=sQuery(id+"F7.wireOp",EDGE,"E101");Q3=makeQuery(id+"F7.imprint","IMPRINT",FACE,{"disambiguationData":[TD([[makeQuery(id+"F7.imprint","IMPRINT",EDGE,{"derivedFrom":subQ0}),-1.0]])]});}
            var Q4;
            {var subQ0=sQuery(id+"F7.wireOp",EDGE,"E104.MirrorCS");Q4=makeQuery(id+"F7.imprint","IMPRINT",FACE,{"disambiguationData":[TD([[makeQuery(id+"F7.imprint","IMPRINT",EDGE,{"derivedFrom":subQ0}),-1.0]])]});}
            extrude(context, id + "F8", {"entities" : qUnion([Q0, Q1, Q2, Q3, Q4]), "operationType" : NewBodyOperationType.ADD, "depth" : 25 * mm, "offsetDistance" : 25.4 * mm});
        }
        {
            var Q0;
            Q0=makeQuery(id+"F8.opExtrude","SWEPT_FACE",FACE,{"disambiguationData":[OSD([sQuery(id+"F7.wireOp",EDGE,"E105.MirrorCS")])]});
            var sketch = newSketch(context, id + "F9", { "sketchPlane" : qUnion([Q0])});
            skCircle(sketch, "E107", {"center": v(-12.62, 26.73) * mm, "radius": 2.25 * mm});
            skCircle(sketch, "E108", {"center": v(-12.62, 26.73) * mm, "radius": 7 * mm});
            skSolve(sketch);
        }
        {
            var Q0;
            {var subQ0=sQuery(id+"F9.wireOp",EDGE,"XvLhFSOE-29xT-WfMq-VxFd-dd6Hbr4nzbNg");var subQ1=sQuery(id+"F7.wireOp",EDGE,"E100.left");var subQ2=makeQuery(id+"F8.opExtrude","CAP_EDGE",EDGE,{"disambiguationData":[OSD([subQ1])],"isStart":false});var subQ3=makeQuery(id+"F9.imprint","INTERSECT",VERTEX,{"derivedFrom":[subQ2,subQ0]});Q0=makeQuery(id+"F9.imprint","IMPRINT",FACE,{"disambiguationData":[TD([[makeQuery(id+"F9.imprint","IMPRINT",EDGE,{"disambiguationData":[TD([[subQ3,-1.0]])],"derivedFrom":subQ0}),-1.0]])]});}
            var Q1;
            {var subQ0=sQuery(id+"F9.wireOp",EDGE,"XvLhFSOE-29xT-WfMq-VxFd-dd6Hbr4nzbNg");var subQ1=sQuery(id+"F7.wireOp",EDGE,"E100.left");var subQ2=makeQuery(id+"F8.opExtrude","CAP_EDGE",EDGE,{"disambiguationData":[OSD([subQ1])],"isStart":false});var subQ3=makeQuery(id+"F9.imprint","INTERSECT",VERTEX,{"derivedFrom":[subQ2,subQ0]});Q1=makeQuery(id+"F9.imprint","IMPRINT",FACE,{"disambiguationData":[TD([[makeQuery(id+"F9.imprint","IMPRINT",EDGE,{"disambiguationData":[TD([[subQ3,1.0]])],"derivedFrom":subQ0}),-1.0]])]});}
            var Q2;
            Q2=makeQuery(id+"F9.imprint","IMPRINT",FACE,{"disambiguationData":[TD([[makeQuery(id+"F9.imprint","IMPRINT",EDGE,{"derivedFrom":sQuery(id+"F9.wireOp",EDGE,"E107")}),1.0]])]});
            var Q3;
            {var subQ0=sQuery(id+"F9.wireOp",EDGE,"E108");var subQ1=sQuery(id+"F7.wireOp",EDGE,"E105.MirrorCS");var subQ2=makeQuery(id+"F8.opExtrude","CAP_EDGE",EDGE,{"disambiguationData":[OSD([subQ1])],"isStart":false});var subQ3=makeQuery(id+"F9.imprint","INTERSECT",VERTEX,{"derivedFrom":[subQ2,subQ0]});Q3=makeQuery(id+"F9.imprint","IMPRINT",FACE,{"disambiguationData":[TD([[makeQuery(id+"F9.imprint","IMPRINT",EDGE,{"disambiguationData":[TD([[subQ3,-1.0]])],"derivedFrom":subQ0}),-1.0]])]});}
            var Q4;
            {var subQ0=sQuery(id+"F9.wireOp",EDGE,"E108");var subQ1=sQuery(id+"F7.wireOp",EDGE,"E105.MirrorCS");var subQ2=makeQuery(id+"F8.opExtrude","CAP_EDGE",EDGE,{"disambiguationData":[OSD([subQ1])],"isStart":false});var subQ3=makeQuery(id+"F9.imprint","INTERSECT",VERTEX,{"derivedFrom":[subQ2,subQ0]});Q4=makeQuery(id+"F9.imprint","IMPRINT",FACE,{"disambiguationData":[TD([[makeQuery(id+"F9.imprint","IMPRINT",EDGE,{"disambiguationData":[TD([[subQ3,1.0]])],"derivedFrom":subQ0}),-1.0]])]});}
            extrude(context, id + "F10", {"entities" : qUnion([Q0, Q1, Q2, Q3, Q4]), "operationType" : NewBodyOperationType.REMOVE, "endBound" : BoundingType.THROUGH_ALL, "oppositeDirection" : true, "depth" : 25.4 * mm, "offsetDistance" : 25.4 * mm});
        }
    });
